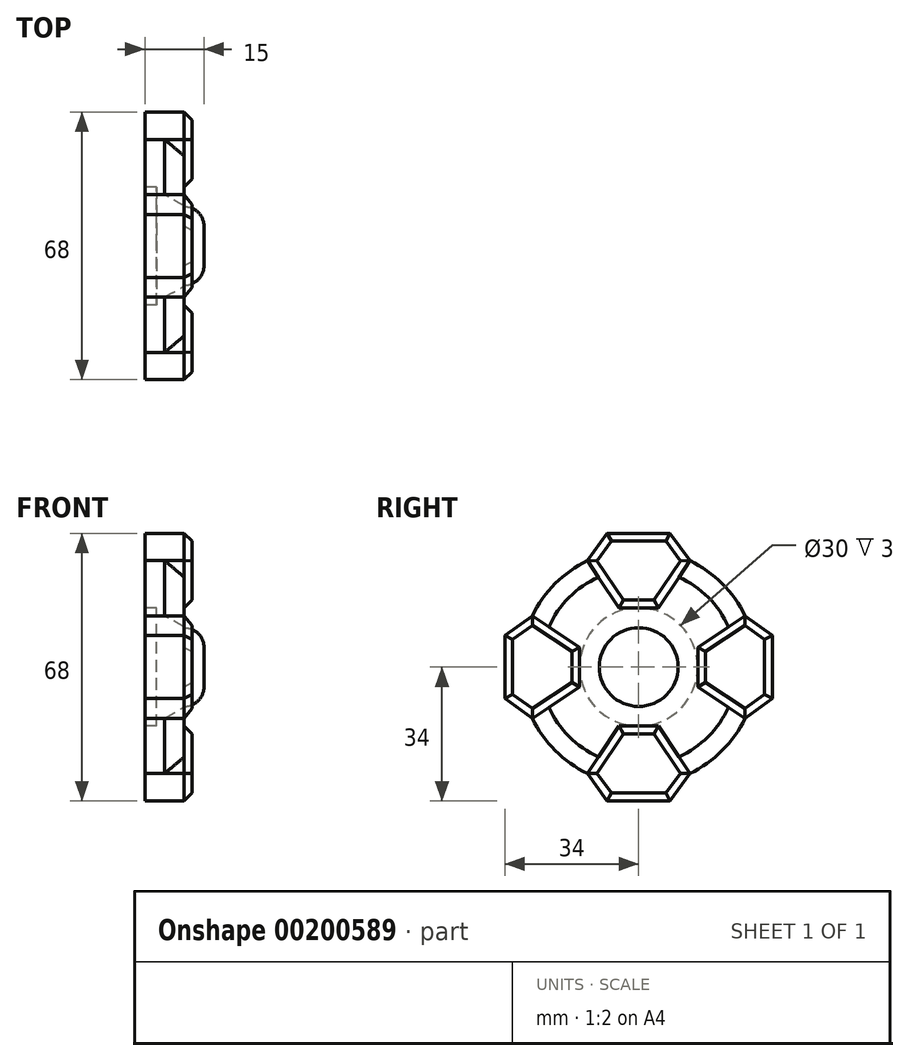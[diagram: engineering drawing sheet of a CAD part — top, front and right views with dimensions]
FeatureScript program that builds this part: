
annotation { "Feature Type Name" : "Feature", "Feature Type Description" : "" }
export const myFeature = defineFeature(function(context is Context, id is Id, definition is map)
    precondition{}
    {
        {
            var Q0;
            Q0=qCreatedBy(makeId("Right.planeOp"),FACE);
            var sketch = newSketch(context, id + "F0", { "sketchPlane" : qUnion([Q0])});
            skCircle(sketch, "E0", {"center": v(0, 0) * mm, "radius": 30 * mm});
            skLineSegment(sketch, "E1", {"start": v(0, 0) * mm, "end": v(0, 30) * mm, "construction": true});
            skLineSegment(sketch, "E2", {"start": v(0, 34) * mm, "end": v(-8, 34) * mm});
            skLineSegment(sketch, "E3", {"start": v(-8, 34) * mm, "end": v(-13, 27.04) * mm});
            skLineSegment(sketch, "E4", {"start": v(-13, 27.04) * mm, "end": v(-5, 15) * mm});
            skLineSegment(sketch, "E5", {"start": v(-5, 15) * mm, "end": v(0, 15) * mm});
            skLineSegment(sketch, "E6.MirrorCS", {"start": v(0, 34) * mm, "end": v(8, 34) * mm});
            skLineSegment(sketch, "E7.MirrorCS", {"start": v(8, 34) * mm, "end": v(13, 27.04) * mm});
            skLineSegment(sketch, "E8.MirrorCS", {"start": v(13, 27.04) * mm, "end": v(5, 15) * mm});
            skLineSegment(sketch, "E9.MirrorCS", {"start": v(5, 15) * mm, "end": v(0, 15) * mm});
            skLineSegment(sketch, "E10.1.0", {"start": v(-34, 8) * mm, "end": v(-27.04, 13) * mm});
            skLineSegment(sketch, "E10.1.1", {"start": v(-34, 0) * mm, "end": v(-34, 8) * mm});
            skLineSegment(sketch, "E10.1.2", {"start": v(-34, 0) * mm, "end": v(-34, -8) * mm});
            skLineSegment(sketch, "E10.1.3", {"start": v(-34, -8) * mm, "end": v(-27.04, -13) * mm});
            skLineSegment(sketch, "E10.1.4", {"start": v(-27.04, -13) * mm, "end": v(-15, -5) * mm});
            skLineSegment(sketch, "E10.1.5", {"start": v(-27.04, 13) * mm, "end": v(-15, 5) * mm});
            skLineSegment(sketch, "E10.1.6", {"start": v(-15, 5) * mm, "end": v(-15, 0) * mm});
            skLineSegment(sketch, "E10.1.7", {"start": v(-15, -5) * mm, "end": v(-15, 0) * mm});
            skLineSegment(sketch, "E10.2.0", {"start": v(-8, -34) * mm, "end": v(-13, -27.04) * mm});
            skLineSegment(sketch, "E10.2.1", {"start": v(0, -34) * mm, "end": v(-8, -34) * mm});
            skLineSegment(sketch, "E10.2.2", {"start": v(0, -34) * mm, "end": v(8, -34) * mm});
            skLineSegment(sketch, "E10.2.3", {"start": v(8, -34) * mm, "end": v(13, -27.04) * mm});
            skLineSegment(sketch, "E10.2.4", {"start": v(13, -27.04) * mm, "end": v(5, -15) * mm});
            skLineSegment(sketch, "E10.2.5", {"start": v(-13, -27.04) * mm, "end": v(-5, -15) * mm});
            skLineSegment(sketch, "E10.2.6", {"start": v(-5, -15) * mm, "end": v(0, -15) * mm});
            skLineSegment(sketch, "E10.2.7", {"start": v(5, -15) * mm, "end": v(0, -15) * mm});
            skLineSegment(sketch, "E10.3.0", {"start": v(34, -8) * mm, "end": v(27.04, -13) * mm});
            skLineSegment(sketch, "E10.3.1", {"start": v(34, 0) * mm, "end": v(34, -8) * mm});
            skLineSegment(sketch, "E10.3.2", {"start": v(34, 0) * mm, "end": v(34, 8) * mm});
            skLineSegment(sketch, "E10.3.3", {"start": v(34, 8) * mm, "end": v(27.04, 13) * mm});
            skLineSegment(sketch, "E10.3.4", {"start": v(27.04, 13) * mm, "end": v(15, 5) * mm});
            skLineSegment(sketch, "E10.3.5", {"start": v(27.04, -13) * mm, "end": v(15, -5) * mm});
            skLineSegment(sketch, "E10.3.6", {"start": v(15, -5) * mm, "end": v(15, 0) * mm});
            skLineSegment(sketch, "E10.3.7", {"start": v(15, 5) * mm, "end": v(15, 0) * mm});
            skSolve(sketch);
        }
        {
            var Q0;
            {var subQ2=sQuery(id+"F0.wireOp",EDGE,"E4");Q0=makeQuery(id+"F0.imprint","IMPRINT",FACE,{"disambiguationData":[TD([[makeQuery(id+"F0.imprint","IMPRINT",EDGE,{"derivedFrom":subQ2}),-1.0]])]});}
            extrude(context, id + "F1", {"entities" : qUnion([Q0]), "depth" : 10 * mm});
        }
        {
            var Q0;
            {var subQ1=sQuery(id+"F0.wireOp",EDGE,"E10.3.4");Q0=makeQuery(id+"F0.imprint","IMPRINT",FACE,{"disambiguationData":[TD([[makeQuery(id+"F0.imprint","IMPRINT",EDGE,{"derivedFrom":subQ1}),1.0]])]});}
            var Q1;
            {var subQ0=sQuery(id+"F0.wireOp",EDGE,"E10.3.0");Q1=makeQuery(id+"F0.imprint","IMPRINT",FACE,{"disambiguationData":[TD([[makeQuery(id+"F0.imprint","IMPRINT",EDGE,{"derivedFrom":subQ0}),-1.0]])]});}
            var Q2;
            {var subQ1=sQuery(id+"F0.wireOp",EDGE,"E4");Q2=makeQuery(id+"F0.imprint","IMPRINT",FACE,{"disambiguationData":[TD([[makeQuery(id+"F0.imprint","IMPRINT",EDGE,{"derivedFrom":subQ1}),1.0]])]});}
            var Q3;
            Q3=makeQuery(id+"F0.imprint","IMPRINT",FACE,{"disambiguationData":[TD([[makeQuery(id+"F0.imprint","IMPRINT",EDGE,{"derivedFrom":sQuery(id+"F0.wireOp",EDGE,"E2")}),1.0]])]});
            var Q4;
            {var subQ1=sQuery(id+"F0.wireOp",EDGE,"E10.1.4");Q4=makeQuery(id+"F0.imprint","IMPRINT",FACE,{"disambiguationData":[TD([[makeQuery(id+"F0.imprint","IMPRINT",EDGE,{"derivedFrom":subQ1}),1.0]])]});}
            var Q5;
            {var subQ0=sQuery(id+"F0.wireOp",EDGE,"E10.1.0");Q5=makeQuery(id+"F0.imprint","IMPRINT",FACE,{"disambiguationData":[TD([[makeQuery(id+"F0.imprint","IMPRINT",EDGE,{"derivedFrom":subQ0}),-1.0]])]});}
            var Q6;
            {var subQ1=sQuery(id+"F0.wireOp",EDGE,"E10.2.4");Q6=makeQuery(id+"F0.imprint","IMPRINT",FACE,{"disambiguationData":[TD([[makeQuery(id+"F0.imprint","IMPRINT",EDGE,{"derivedFrom":subQ1}),1.0]])]});}
            var Q7;
            {var subQ0=sQuery(id+"F0.wireOp",EDGE,"E10.2.0");Q7=makeQuery(id+"F0.imprint","IMPRINT",FACE,{"disambiguationData":[TD([[makeQuery(id+"F0.imprint","IMPRINT",EDGE,{"derivedFrom":subQ0}),-1.0]])]});}
            extrude(context, id + "F2", {"entities" : qUnion([Q0, Q1, Q2, Q3, Q4, Q5, Q6, Q7]), "operationType" : NewBodyOperationType.ADD, "depth" : 12 * mm});
        }
        {
            var Q0;
            {var subQ0=sQuery(id+"F0.wireOp",EDGE,"E0");Q0=makeQuery(id+"F1.opExtrude","CAP_EDGE",EDGE,{"disambiguationData":[OSD([subQ0]),TDD([makeQuery(id+"F0.imprint","IMPRINT",EDGE,{"disambiguationData":[TD([[makeQuery(id+"F0.imprint","INTERSECT",VERTEX,{"derivedFrom":[subQ0,sQuery(id+"F0.wireOp",EDGE,"E7.MirrorCS"),sQuery(id+"F0.wireOp",EDGE,"E8.MirrorCS")]}),1.0]])],"derivedFrom":subQ0})])],"isStart":false});}
            var Q1;
            {var subQ0=sQuery(id+"F0.wireOp",EDGE,"E0");Q1=makeQuery(id+"F1.opExtrude","CAP_EDGE",EDGE,{"disambiguationData":[OSD([subQ0]),TDD([makeQuery(id+"F0.imprint","IMPRINT",EDGE,{"disambiguationData":[TD([[makeQuery(id+"F0.imprint","INTERSECT",VERTEX,{"derivedFrom":[subQ0,sQuery(id+"F0.wireOp",EDGE,"E3"),sQuery(id+"F0.wireOp",EDGE,"E4")]}),-1.0]])],"derivedFrom":subQ0})])],"isStart":false});}
            var Q2;
            {var subQ0=sQuery(id+"F0.wireOp",EDGE,"E0");Q2=makeQuery(id+"F1.opExtrude","CAP_EDGE",EDGE,{"disambiguationData":[OSD([subQ0]),TDD([makeQuery(id+"F0.imprint","IMPRINT",EDGE,{"disambiguationData":[TD([[makeQuery(id+"F0.imprint","INTERSECT",VERTEX,{"derivedFrom":[subQ0,sQuery(id+"F0.wireOp",EDGE,"E10.1.3"),sQuery(id+"F0.wireOp",EDGE,"E10.1.4")]}),-1.0]])],"derivedFrom":subQ0})])],"isStart":false});}
            var Q3;
            {var subQ0=sQuery(id+"F0.wireOp",EDGE,"E0");Q3=makeQuery(id+"F1.opExtrude","CAP_EDGE",EDGE,{"disambiguationData":[OSD([subQ0]),TDD([makeQuery(id+"F0.imprint","IMPRINT",EDGE,{"disambiguationData":[TD([[makeQuery(id+"F0.imprint","INTERSECT",VERTEX,{"derivedFrom":[subQ0,sQuery(id+"F0.wireOp",EDGE,"E10.2.3"),sQuery(id+"F0.wireOp",EDGE,"E10.2.4")]}),-1.0]])],"derivedFrom":subQ0})])],"isStart":false});}
            chamfer(context, id + "F3", {"entities" : qUnion([Q0, Q1, Q2, Q3]), "width" : 5 * mm, "tangentPropagation" : true});
        }
        {
            var Q0;
            Q0=makeQuery(id+"F2.opExtrude","CAP_EDGE",EDGE,{"disambiguationData":[OSD([sQuery(id+"F0.wireOp",EDGE,"E2"),sQuery(id+"F0.wireOp",EDGE,"E6.MirrorCS")])],"isStart":false});
            var Q1;
            Q1=makeQuery(id+"F2.opExtrude","CAP_EDGE",EDGE,{"disambiguationData":[OSD([sQuery(id+"F0.wireOp",EDGE,"E3")])],"isStart":false});
            var Q2;
            Q2=makeQuery(id+"F2.opExtrude","CAP_EDGE",EDGE,{"disambiguationData":[OSD([sQuery(id+"F0.wireOp",EDGE,"E7.MirrorCS")])],"isStart":false});
            var Q3;
            Q3=makeQuery(id+"F2.opExtrude","CAP_EDGE",EDGE,{"disambiguationData":[OSD([sQuery(id+"F0.wireOp",EDGE,"E4")])],"isStart":false});
            var Q4;
            Q4=makeQuery(id+"F2.opExtrude","CAP_EDGE",EDGE,{"disambiguationData":[OSD([sQuery(id+"F0.wireOp",EDGE,"E8.MirrorCS")])],"isStart":false});
            var Q5;
            Q5=makeQuery(id+"F2.opExtrude","CAP_EDGE",EDGE,{"disambiguationData":[OSD([sQuery(id+"F0.wireOp",EDGE,"E5"),sQuery(id+"F0.wireOp",EDGE,"E9.MirrorCS")])],"isStart":false});
            var Q6;
            Q6=makeQuery(id+"F2.opExtrude","CAP_EDGE",EDGE,{"disambiguationData":[OSD([sQuery(id+"F0.wireOp",EDGE,"E10.1.6"),sQuery(id+"F0.wireOp",EDGE,"E10.1.7")])],"isStart":false});
            var Q7;
            Q7=makeQuery(id+"F2.opExtrude","CAP_EDGE",EDGE,{"disambiguationData":[OSD([sQuery(id+"F0.wireOp",EDGE,"E10.1.5")])],"isStart":false});
            var Q8;
            Q8=makeQuery(id+"F2.opExtrude","CAP_EDGE",EDGE,{"disambiguationData":[OSD([sQuery(id+"F0.wireOp",EDGE,"E10.1.0")])],"isStart":false});
            var Q9;
            Q9=makeQuery(id+"F2.opExtrude","CAP_EDGE",EDGE,{"disambiguationData":[OSD([sQuery(id+"F0.wireOp",EDGE,"E10.1.1"),sQuery(id+"F0.wireOp",EDGE,"E10.1.2")])],"isStart":false});
            var Q10;
            Q10=makeQuery(id+"F2.opExtrude","CAP_EDGE",EDGE,{"disambiguationData":[OSD([sQuery(id+"F0.wireOp",EDGE,"E10.1.3")])],"isStart":false});
            var Q11;
            Q11=makeQuery(id+"F2.opExtrude","CAP_EDGE",EDGE,{"disambiguationData":[OSD([sQuery(id+"F0.wireOp",EDGE,"E10.1.4")])],"isStart":false});
            var Q12;
            Q12=makeQuery(id+"F2.opExtrude","CAP_EDGE",EDGE,{"disambiguationData":[OSD([sQuery(id+"F0.wireOp",EDGE,"E10.2.6"),sQuery(id+"F0.wireOp",EDGE,"E10.2.7")])],"isStart":false});
            var Q13;
            Q13=makeQuery(id+"F2.opExtrude","CAP_EDGE",EDGE,{"disambiguationData":[OSD([sQuery(id+"F0.wireOp",EDGE,"E10.2.5")])],"isStart":false});
            var Q14;
            Q14=makeQuery(id+"F2.opExtrude","CAP_EDGE",EDGE,{"disambiguationData":[OSD([sQuery(id+"F0.wireOp",EDGE,"E10.2.0")])],"isStart":false});
            var Q15;
            Q15=makeQuery(id+"F2.opExtrude","CAP_EDGE",EDGE,{"disambiguationData":[OSD([sQuery(id+"F0.wireOp",EDGE,"E10.2.1"),sQuery(id+"F0.wireOp",EDGE,"E10.2.2")])],"isStart":false});
            var Q16;
            Q16=makeQuery(id+"F2.opExtrude","CAP_EDGE",EDGE,{"disambiguationData":[OSD([sQuery(id+"F0.wireOp",EDGE,"E10.2.3")])],"isStart":false});
            var Q17;
            Q17=makeQuery(id+"F2.opExtrude","CAP_EDGE",EDGE,{"disambiguationData":[OSD([sQuery(id+"F0.wireOp",EDGE,"E10.2.4")])],"isStart":false});
            var Q18;
            Q18=makeQuery(id+"F2.opExtrude","CAP_EDGE",EDGE,{"disambiguationData":[OSD([sQuery(id+"F0.wireOp",EDGE,"E10.3.6"),sQuery(id+"F0.wireOp",EDGE,"E10.3.7")])],"isStart":false});
            var Q19;
            Q19=makeQuery(id+"F2.opExtrude","CAP_EDGE",EDGE,{"disambiguationData":[OSD([sQuery(id+"F0.wireOp",EDGE,"E10.3.4")])],"isStart":false});
            var Q20;
            Q20=makeQuery(id+"F2.opExtrude","CAP_EDGE",EDGE,{"disambiguationData":[OSD([sQuery(id+"F0.wireOp",EDGE,"E10.3.3")])],"isStart":false});
            var Q21;
            Q21=makeQuery(id+"F2.opExtrude","CAP_EDGE",EDGE,{"disambiguationData":[OSD([sQuery(id+"F0.wireOp",EDGE,"E10.3.1"),sQuery(id+"F0.wireOp",EDGE,"E10.3.2")])],"isStart":false});
            var Q22;
            Q22=makeQuery(id+"F2.opExtrude","CAP_EDGE",EDGE,{"disambiguationData":[OSD([sQuery(id+"F0.wireOp",EDGE,"E10.3.5")])],"isStart":false});
            var Q23;
            Q23=makeQuery(id+"F2.opExtrude","CAP_EDGE",EDGE,{"disambiguationData":[OSD([sQuery(id+"F0.wireOp",EDGE,"E10.3.0")])],"isStart":false});
            chamfer(context, id + "F4", {"entities" : qUnion([Q0, Q1, Q2, Q3, Q4, Q5, Q6, Q7, Q8, Q9, Q10, Q11, Q12, Q13, Q14, Q15, Q16, Q17, Q18, Q19, Q20, Q21, Q22, Q23]), "width" : 2 * mm, "tangentPropagation" : true});
        }
        {
            var Q0;
            Q0=makeQuery(id+"F1.opExtrude","CAP_FACE",FACE,{"disambiguationData":[OSD([sQuery(id+"F0.wireOp",EDGE,"E0"),sQuery(id+"F0.wireOp",EDGE,"E4"),sQuery(id+"F0.wireOp",EDGE,"E5"),sQuery(id+"F0.wireOp",EDGE,"E8.MirrorCS"),sQuery(id+"F0.wireOp",EDGE,"E9.MirrorCS"),sQuery(id+"F0.wireOp",EDGE,"E10.1.4"),sQuery(id+"F0.wireOp",EDGE,"E10.1.5"),sQuery(id+"F0.wireOp",EDGE,"E10.1.6"),sQuery(id+"F0.wireOp",EDGE,"E10.1.7"),sQuery(id+"F0.wireOp",EDGE,"E10.2.4"),sQuery(id+"F0.wireOp",EDGE,"E10.2.5"),sQuery(id+"F0.wireOp",EDGE,"E10.2.6"),sQuery(id+"F0.wireOp",EDGE,"E10.2.7"),sQuery(id+"F0.wireOp",EDGE,"E10.3.4"),sQuery(id+"F0.wireOp",EDGE,"E10.3.5"),sQuery(id+"F0.wireOp",EDGE,"E10.3.6"),sQuery(id+"F0.wireOp",EDGE,"E10.3.7")])],"isStart":false});
            var sketch = newSketch(context, id + "F5", { "sketchPlane" : qUnion([Q0])});
            skCircle(sketch, "E11", {"center": v(0, 0) * mm, "radius": 10 * mm});
            skSolve(sketch);
        }
        {
            var Q0;
            Q0=makeQuery(id+"F5.imprint","IMPRINT",FACE,{"disambiguationData":[TD([[makeQuery(id+"F5.imprint","IMPRINT",EDGE,{"derivedFrom":sQuery(id+"F5.wireOp",EDGE,"E11")}),1.0]])]});
            extrude(context, id + "F6", {"entities" : qUnion([Q0]), "depth" : 5 * mm});
        }
        {
            var Q0;
            Q0=makeQuery(id+"F6.opExtrude","CAP_EDGE",EDGE,{"disambiguationData":[OSD([sQuery(id+"F5.wireOp",EDGE,"E11")])],"isStart":false});
            fillet(context, id + "F7", {"entities" : qUnion([Q0]), "radius" : 5 * mm, "tangentPropagation" : true, "allowEdgeOverflow" : false});
        }
        {
            var Q0;
            {var subQ2=sQuery(id+"F0.wireOp",EDGE,"E4");Q0=makeQuery(id+"F0.imprint","IMPRINT",FACE,{"disambiguationData":[TD([[makeQuery(id+"F0.imprint","IMPRINT",EDGE,{"derivedFrom":subQ2}),-1.0]])]});}
            var sketch = newSketch(context, id + "F8", { "sketchPlane" : qUnion([Q0])});
            skCircle(sketch, "E12", {"center": v(0, 0) * mm, "radius": 15 * mm});
            skSolve(sketch);
        }
        {
            var Q0;
            {var subQ0=sQuery(id+"F8.wireOp",EDGE,"E12");var subQ1=makeQuery(id+"F8.imprint","INTERSECT",VERTEX,{"derivedFrom":[makeQuery(id+"F0.imprint","IMPRINT",EDGE,{"derivedFrom":sQuery(id+"F0.wireOp",EDGE,"E5")}),makeQuery(id+"F0.imprint","IMPRINT",EDGE,{"derivedFrom":sQuery(id+"F0.wireOp",EDGE,"E9.MirrorCS")}),subQ0]});Q0=makeQuery(id+"F8.imprint","IMPRINT",FACE,{"disambiguationData":[TD([[makeQuery(id+"F8.imprint","IMPRINT",EDGE,{"disambiguationData":[TD([[subQ1,1.0]])],"derivedFrom":subQ0}),1.0]])]});}
            extrude(context, id + "F9", {"entities" : qUnion([Q0]), "operationType" : NewBodyOperationType.REMOVE, "depth" : 3 * mm});
        }
    });
